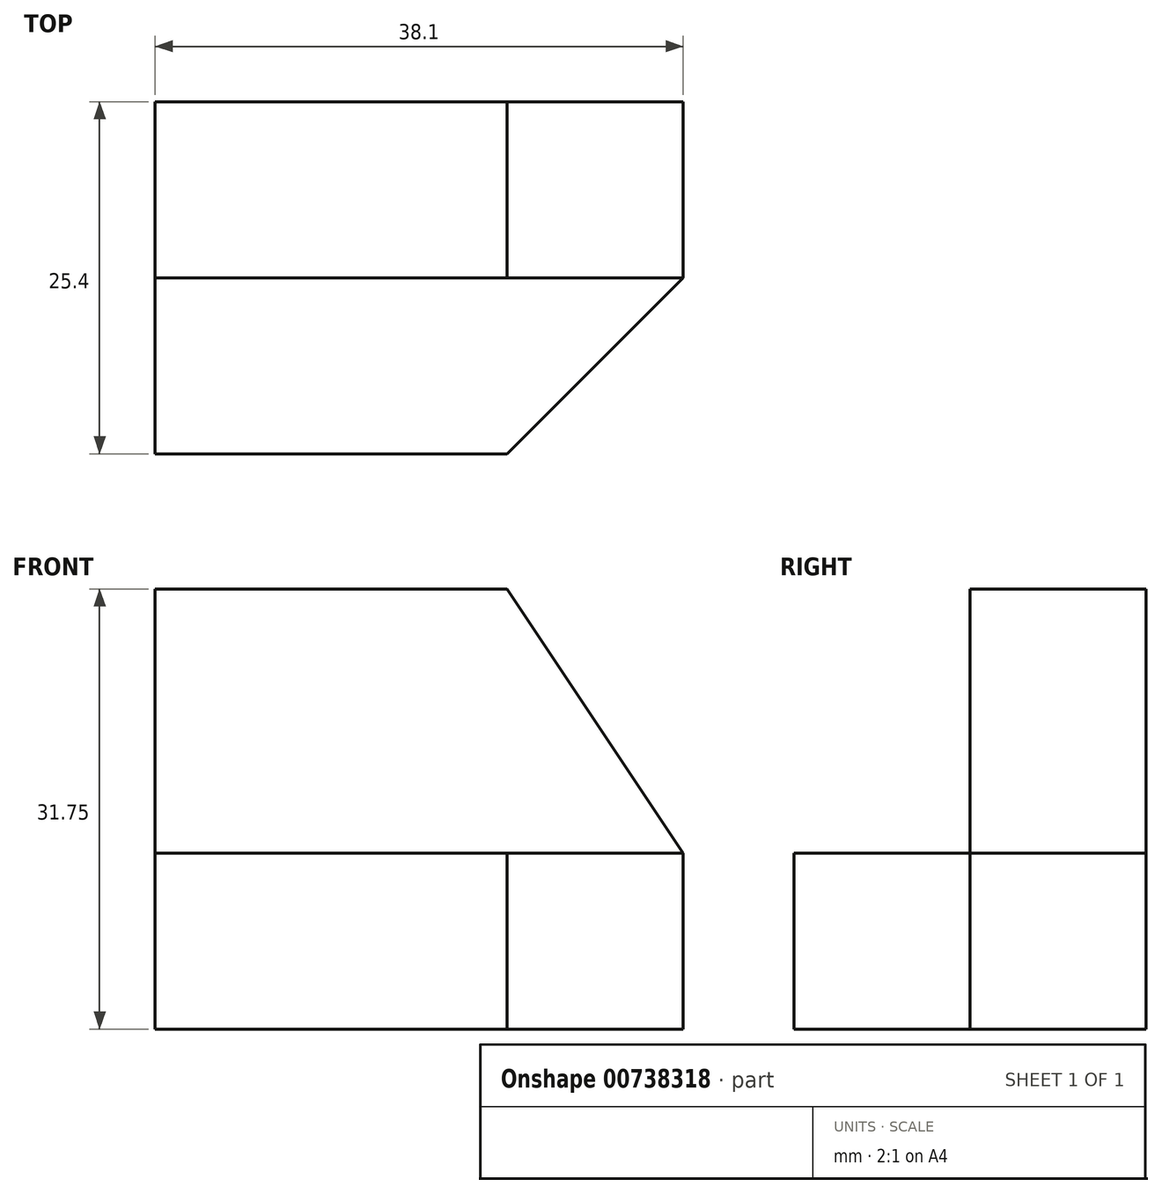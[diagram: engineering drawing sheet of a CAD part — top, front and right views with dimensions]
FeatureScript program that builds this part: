
annotation { "Feature Type Name" : "Feature", "Feature Type Description" : "" }
export const myFeature = defineFeature(function(context is Context, id is Id, definition is map)
    precondition{}
    {
        {
            var Q0;
            Q0=qCreatedBy(makeId("Front.planeOp"),FACE);
            var sketch = newSketch(context, id + "F0", { "sketchPlane" : qUnion([Q0])});
            skLineSegment(sketch, "E0", {"start": v(-38.1, 0) * mm, "end": v(-38.1, 31.75) * mm});
            skLineSegment(sketch, "E1", {"start": v(-38.1, 31.75) * mm, "end": v(0, 31.75) * mm});
            skLineSegment(sketch, "E2", {"start": v(0, 31.75) * mm, "end": v(0, 0) * mm});
            skLineSegment(sketch, "E3", {"start": v(0, 0) * mm, "end": v(-38.1, 0) * mm});
            skSolve(sketch);
        }
        {
            var Q0;
            Q0=makeQuery(id+"F0.imprint","IMPRINT",FACE,{"disambiguationData":[TD([[makeQuery(id+"F0.imprint","IMPRINT",EDGE,{"derivedFrom":sQuery(id+"F0.wireOp",EDGE,"E0")}),-1.0]])]});
            extrude(context, id + "F1", {"entities" : qUnion([Q0]), "depth" : 25.4 * mm, "offsetDistance" : 25.4 * mm});
        }
        {
            var Q0;
            Q0=makeQuery(id+"F1.opExtrude","SWEPT_FACE",FACE,{"disambiguationData":[OSD([sQuery(id+"F0.wireOp",EDGE,"E2")])]});
            var sketch = newSketch(context, id + "F2", { "sketchPlane" : qUnion([Q0])});
            skLineSegment(sketch, "E4", {"start": v(-25.4, 12.7) * mm, "end": v(-12.7, 12.7) * mm});
            skLineSegment(sketch, "E5", {"start": v(-12.7, 12.7) * mm, "end": v(-12.7, 31.75) * mm});
            skLineSegment(sketch, "E6", {"start": v(-12.7, 31.75) * mm, "end": v(0, 31.75) * mm});
            skSolve(sketch);
        }
        {
            var Q0;
            {var subQ0=sQuery(id+"F2.wireOp",EDGE,"E4");Q0=makeQuery(id+"F2.imprint","IMPRINT",FACE,{"disambiguationData":[TD([[makeQuery(id+"F2.imprint","IMPRINT",EDGE,{"derivedFrom":subQ0}),1.0]])]});}
            extrude(context, id + "F3", {"entities" : qUnion([Q0]), "operationType" : NewBodyOperationType.REMOVE, "endBound" : BoundingType.THROUGH_ALL, "oppositeDirection" : true, "depth" : 25.4 * mm, "offsetDistance" : 25.4 * mm});
        }
        {
            var Q0;
            Q0=makeQuery(id+"F3.boolean.opBoolean","COPY",FACE,{"derivedFrom":makeQuery(id+"F3.opExtrude","SWEPT_FACE",FACE,{"disambiguationData":[OSD([sQuery(id+"F2.wireOp",EDGE,"E5")])]})});
            var sketch = newSketch(context, id + "F4", { "sketchPlane" : qUnion([Q0])});
            skLineSegment(sketch, "E7", {"start": v(-12.7, 31.75) * mm, "end": v(0, 12.7) * mm});
            skLineSegment(sketch, "E8", {"start": v(-12.7, 31.75) * mm, "end": v(0, 31.75) * mm});
            skSolve(sketch);
        }
        {
            var Q0;
            Q0=makeQuery(id+"F4.imprint","IMPRINT",FACE,{"disambiguationData":[TD([[makeQuery(id+"F4.imprint","IMPRINT",EDGE,{"derivedFrom":sQuery(id+"F4.wireOp",EDGE,"E7")}),1.0]])]});
            extrude(context, id + "F5", {"entities" : qUnion([Q0]), "operationType" : NewBodyOperationType.REMOVE, "endBound" : BoundingType.THROUGH_ALL, "oppositeDirection" : true, "depth" : 25.4 * mm, "offsetDistance" : 25.4 * mm});
        }
        {
            var Q0;
            Q0=makeQuery(id+"F3.boolean.opBoolean","COPY",FACE,{"derivedFrom":makeQuery(id+"F3.opExtrude","SWEPT_FACE",FACE,{"disambiguationData":[OSD([sQuery(id+"F2.wireOp",EDGE,"E4")])]})});
            var sketch = newSketch(context, id + "F6", { "sketchPlane" : qUnion([Q0])});
            skLineSegment(sketch, "E9", {"start": v(0, -12.7) * mm, "end": v(-12.7, -25.4) * mm});
            skLineSegment(sketch, "E10", {"start": v(-12.7, -25.4) * mm, "end": v(0, -25.4) * mm});
            skSolve(sketch);
        }
        {
            var Q0;
            Q0=makeQuery(id+"F6.imprint","IMPRINT",FACE,{"disambiguationData":[TD([[makeQuery(id+"F6.imprint","IMPRINT",EDGE,{"derivedFrom":sQuery(id+"F6.wireOp",EDGE,"E9")}),1.0]])]});
            extrude(context, id + "F7", {"entities" : qUnion([Q0]), "operationType" : NewBodyOperationType.REMOVE, "endBound" : BoundingType.THROUGH_ALL, "oppositeDirection" : true, "depth" : 25.4 * mm, "offsetDistance" : 25.4 * mm});
        }
    });
